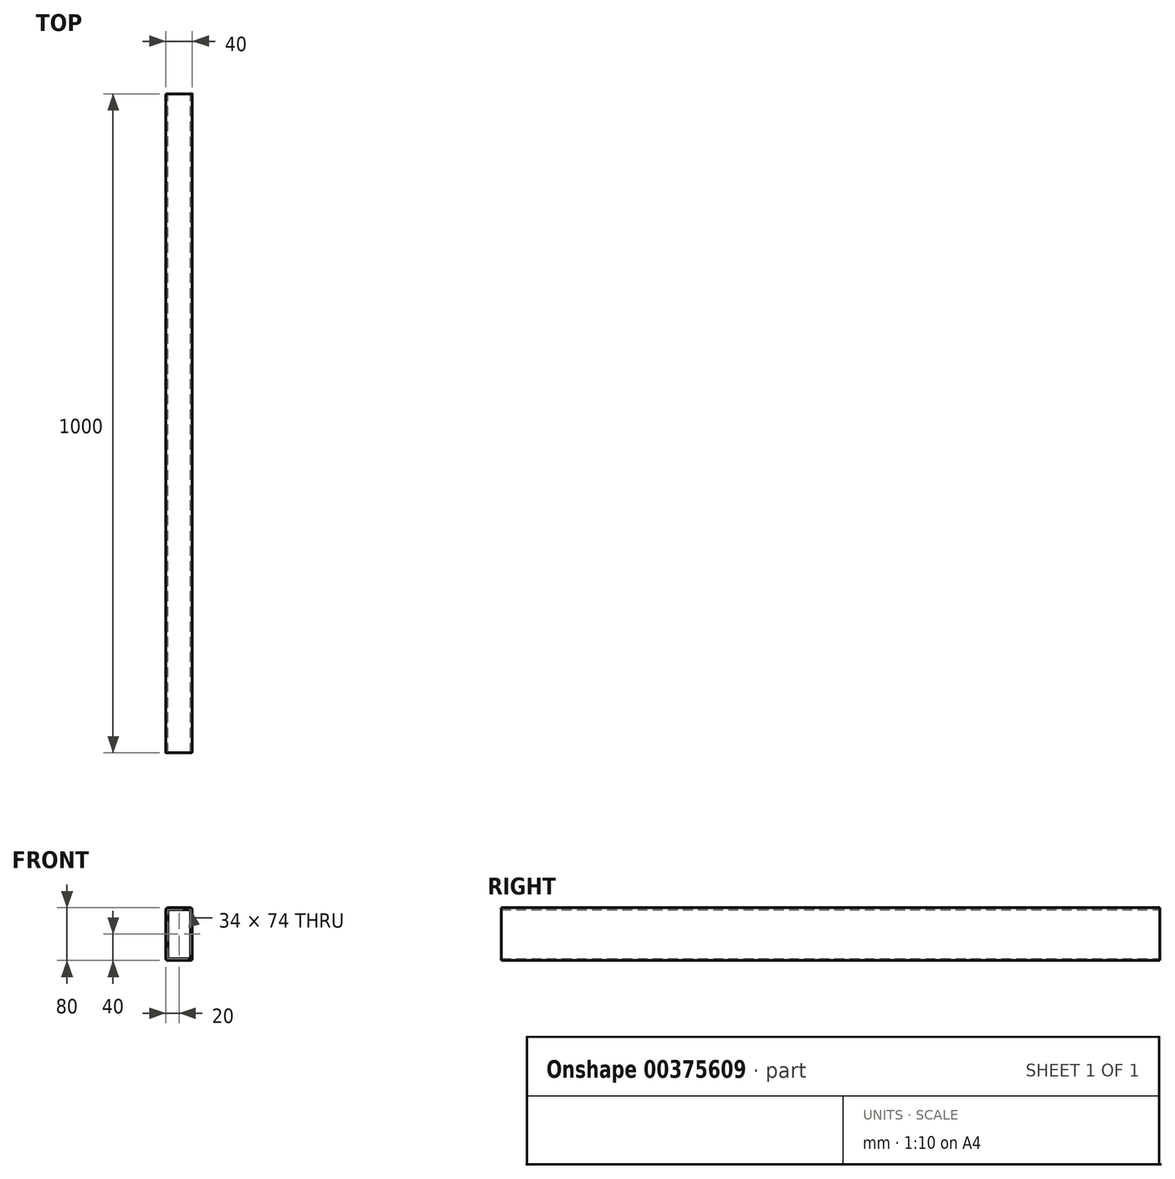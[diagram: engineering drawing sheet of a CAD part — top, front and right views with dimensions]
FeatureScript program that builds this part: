
annotation { "Feature Type Name" : "Feature", "Feature Type Description" : "" }
export const myFeature = defineFeature(function(context is Context, id is Id, definition is map)
    precondition{}
    {
        {
            var Q0;
            Q0=qCreatedBy(makeId("Front.planeOp"),FACE);
            var sketch = newSketch(context, id + "F0", { "sketchPlane" : qUnion([Q0])});
            skLineSegment(sketch, "E0.bottom", {"start": v(17, -40) * mm, "end": v(-17, -40) * mm});
            skLineSegment(sketch, "E0.top", {"start": v(17, 40) * mm, "end": v(-17, 40) * mm});
            skLineSegment(sketch, "E0.left", {"start": v(20, -37) * mm, "end": v(20, 37) * mm});
            skLineSegment(sketch, "E0.right", {"start": v(-20, -37) * mm, "end": v(-20, 37) * mm});
            skPoint(sketch, "E0.middle", {"position": v(0, 0) * mm});
            skPoint(sketch, "E1.visualSharp", {"position": v(-20, 40) * mm});
            skArc(sketch, "E1.filletArc", {"start": v(-17, 40) * mm, "mid": v(-19.12, 39.12) * mm, "end": v(-20, 37) * mm});
            skPoint(sketch, "E2.visualSharp", {"position": v(20, 40) * mm});
            skArc(sketch, "E2.filletArc", {"start": v(20, 37) * mm, "mid": v(19.12, 39.12) * mm, "end": v(17, 40) * mm});
            skPoint(sketch, "E3.visualSharp", {"position": v(20, -40) * mm});
            skArc(sketch, "E3.filletArc", {"start": v(17, -40) * mm, "mid": v(19.12, -39.12) * mm, "end": v(20, -37) * mm});
            skPoint(sketch, "E4.visualSharp", {"position": v(-20, -40) * mm});
            skArc(sketch, "E4.filletArc", {"start": v(-20, -37) * mm, "mid": v(-19.12, -39.12) * mm, "end": v(-17, -40) * mm});
            skLineSegment(sketch, "E5.0", {"start": v(17, -37) * mm, "end": v(17, 37) * mm});
            skLineSegment(sketch, "E5.1", {"start": v(17, -37) * mm, "end": v(-17, -37) * mm});
            skLineSegment(sketch, "E5.2", {"start": v(-17, -37) * mm, "end": v(-17, 37) * mm});
            skLineSegment(sketch, "E5.3", {"start": v(17, 37) * mm, "end": v(-17, 37) * mm});
            skSolve(sketch);
        }
        {
            var Q0;
            Q0 = qSketchRegion(id + "F0", true);
            extrude(context, id + "F1", {"entities" : qUnion([Q0]), "depth" : 1000 * mm});
        }
    });
